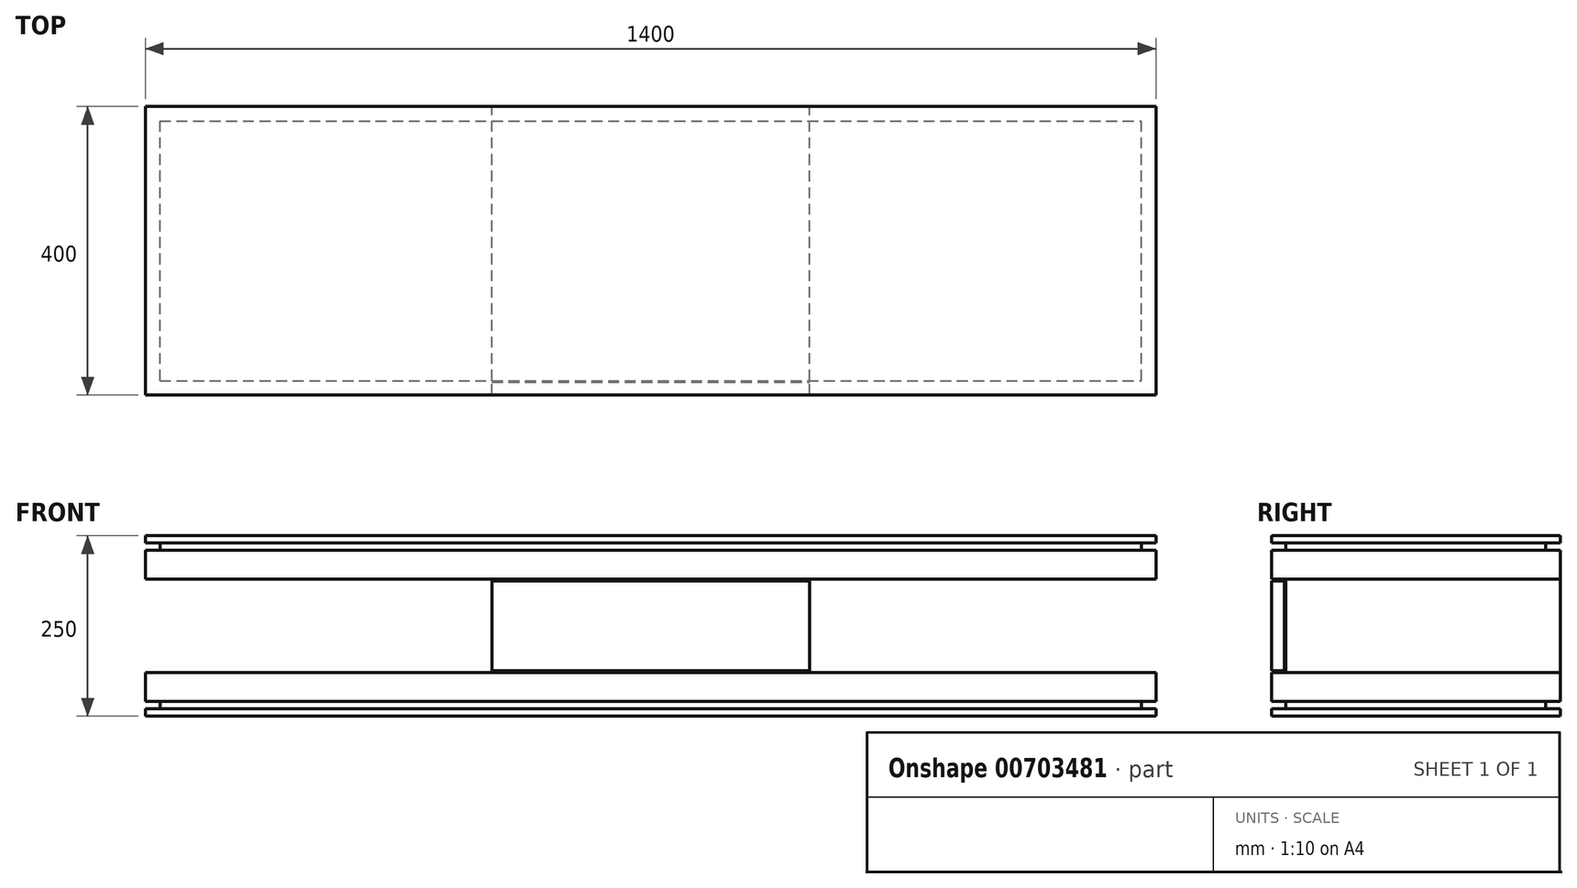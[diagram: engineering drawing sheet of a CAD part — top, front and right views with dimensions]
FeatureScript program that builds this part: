
annotation { "Feature Type Name" : "Feature", "Feature Type Description" : "" }
export const myFeature = defineFeature(function(context is Context, id is Id, definition is map)
    precondition{}
    {
        {
            var Q0;
            Q0=qCreatedBy(makeId("Front.planeOp"),FACE);
            var sketch = newSketch(context, id + "F0", { "sketchPlane" : qUnion([Q0])});
            skLineSegment(sketch, "E0.bottom", {"start": v(-700, 10) * mm, "end": v(700, 10) * mm});
            skLineSegment(sketch, "E0.top", {"start": v(-700, 0) * mm, "end": v(700, 0) * mm});
            skLineSegment(sketch, "E0.left", {"start": v(-700, 10) * mm, "end": v(-700, 0) * mm});
            skLineSegment(sketch, "E0.right", {"start": v(700, 10) * mm, "end": v(700, 0) * mm});
            skLineSegment(sketch, "E1.bottom", {"start": v(-680, 20) * mm, "end": v(680, 20) * mm});
            skLineSegment(sketch, "E1.top", {"start": v(-680, 10) * mm, "end": v(680, 10) * mm});
            skLineSegment(sketch, "E1.left", {"start": v(-680, 20) * mm, "end": v(-680, 10) * mm});
            skLineSegment(sketch, "E1.right", {"start": v(680, 20) * mm, "end": v(680, 10) * mm});
            skLineSegment(sketch, "E2", {"start": v(0, 20) * mm, "end": v(0, 10) * mm});
            skLineSegment(sketch, "E3.bottom", {"start": v(-700, 60) * mm, "end": v(700, 60) * mm});
            skLineSegment(sketch, "E3.top", {"start": v(-700, 20) * mm, "end": v(700, 20) * mm});
            skLineSegment(sketch, "E3.left", {"start": v(-700, 60) * mm, "end": v(-700, 20) * mm});
            skLineSegment(sketch, "E3.right", {"start": v(700, 60) * mm, "end": v(700, 20) * mm});
            skLineSegment(sketch, "E4", {"start": v(0, 20) * mm, "end": v(0, 60) * mm});
            skLineSegment(sketch, "E5.bottom", {"start": v(-700, 60) * mm, "end": v(-660, 60) * mm});
            skLineSegment(sketch, "E5.top", {"start": v(-700, 190) * mm, "end": v(-660, 190) * mm});
            skLineSegment(sketch, "E5.left", {"start": v(-700, 60) * mm, "end": v(-700, 190) * mm});
            skLineSegment(sketch, "E5.right", {"start": v(-660, 60) * mm, "end": v(-660, 190) * mm});
            skLineSegment(sketch, "E6.bottom", {"start": v(700, 60) * mm, "end": v(660, 60) * mm});
            skLineSegment(sketch, "E6.top", {"start": v(700, 190) * mm, "end": v(660, 190) * mm});
            skLineSegment(sketch, "E6.left", {"start": v(700, 60) * mm, "end": v(700, 190) * mm});
            skLineSegment(sketch, "E6.right", {"start": v(660, 60) * mm, "end": v(660, 190) * mm});
            skLineSegment(sketch, "E7.bottom", {"start": v(-700, 190) * mm, "end": v(700, 190) * mm});
            skLineSegment(sketch, "E7.top", {"start": v(-700, 230) * mm, "end": v(700, 230) * mm});
            skLineSegment(sketch, "E7.left", {"start": v(-700, 190) * mm, "end": v(-700, 230) * mm});
            skLineSegment(sketch, "E7.right", {"start": v(700, 190) * mm, "end": v(700, 230) * mm});
            skLineSegment(sketch, "E8.bottom", {"start": v(-680, 240) * mm, "end": v(680, 240) * mm});
            skLineSegment(sketch, "E8.top", {"start": v(-680, 230) * mm, "end": v(680, 230) * mm});
            skLineSegment(sketch, "E8.left", {"start": v(-680, 240) * mm, "end": v(-680, 230) * mm});
            skLineSegment(sketch, "E8.right", {"start": v(680, 240) * mm, "end": v(680, 230) * mm});
            skLineSegment(sketch, "E9", {"start": v(0, 240) * mm, "end": v(0, 230) * mm});
            skLineSegment(sketch, "E10.bottom", {"start": v(-700, 250) * mm, "end": v(700, 250) * mm});
            skLineSegment(sketch, "E10.top", {"start": v(-700, 240) * mm, "end": v(700, 240) * mm});
            skLineSegment(sketch, "E10.left", {"start": v(-700, 250) * mm, "end": v(-700, 240) * mm});
            skLineSegment(sketch, "E10.right", {"start": v(700, 250) * mm, "end": v(700, 240) * mm});
            skLineSegment(sketch, "E11", {"start": v(0, 250) * mm, "end": v(0, 240) * mm});
            skLineSegment(sketch, "E12", {"start": v(-660, 125) * mm, "end": v(-220, 125) * mm, "construction": true});
            skLineSegment(sketch, "E13", {"start": v(-220, 125) * mm, "end": v(220, 125) * mm, "construction": true});
            skLineSegment(sketch, "E14", {"start": v(220, 125) * mm, "end": v(660, 125) * mm, "construction": true});
            skLineSegment(sketch, "E15", {"start": v(-220, 190) * mm, "end": v(-220, 60) * mm});
            skLineSegment(sketch, "E16", {"start": v(220, 190) * mm, "end": v(220, 60) * mm});
            skLineSegment(sketch, "E17", {"start": v(-220, 187) * mm, "end": v(220, 187) * mm});
            skLineSegment(sketch, "E18", {"start": v(-220, 63) * mm, "end": v(220, 63) * mm});
            skSolve(sketch);
        }
        {
            var Q0;
            {var subQ0=sQuery(id+"F0.wireOp",EDGE,"E8.left");Q0=makeQuery(id+"F0.imprint","IMPRINT",FACE,{"disambiguationData":[TD([[makeQuery(id+"F0.imprint","IMPRINT",EDGE,{"derivedFrom":subQ0}),1.0]])]});}
            var Q1;
            {var subQ0=sQuery(id+"F0.wireOp",EDGE,"E8.right");Q1=makeQuery(id+"F0.imprint","IMPRINT",FACE,{"disambiguationData":[TD([[makeQuery(id+"F0.imprint","IMPRINT",EDGE,{"derivedFrom":subQ0}),-1.0]])]});}
            var Q2;
            {var subQ0=sQuery(id+"F0.wireOp",EDGE,"E1.left");Q2=makeQuery(id+"F0.imprint","IMPRINT",FACE,{"disambiguationData":[TD([[makeQuery(id+"F0.imprint","IMPRINT",EDGE,{"derivedFrom":subQ0}),1.0]])]});}
            var Q3;
            {var subQ0=sQuery(id+"F0.wireOp",EDGE,"E1.right");Q3=makeQuery(id+"F0.imprint","IMPRINT",FACE,{"disambiguationData":[TD([[makeQuery(id+"F0.imprint","IMPRINT",EDGE,{"derivedFrom":subQ0}),-1.0]])]});}
            extrude(context, id + "F1", {"entities" : qUnion([Q0, Q1, Q2, Q3]), "depth" : 180 * mm, "offsetDistance" : 25 * mm, "hasSecondDirection" : true, "secondDirectionOppositeDirection" : true, "secondDirectionDepth" : 180 * mm});
        }
        {
            var Q0;
            Q0=makeQuery(id+"F0.imprint","IMPRINT",FACE,{"disambiguationData":[TD([[makeQuery(id+"F0.imprint","IMPRINT",EDGE,{"derivedFrom":sQuery(id+"F0.wireOp",EDGE,"E0.top")}),1.0]])]});
            var Q1;
            Q1=makeQuery(id+"F0.imprint","IMPRINT",FACE,{"disambiguationData":[TD([[makeQuery(id+"F0.imprint","IMPRINT",EDGE,{"derivedFrom":sQuery(id+"F0.wireOp",EDGE,"E5.bottom")}),1.0]])]});
            var Q2;
            Q2=makeQuery(id+"F0.imprint","IMPRINT",FACE,{"disambiguationData":[TD([[makeQuery(id+"F0.imprint","IMPRINT",EDGE,{"derivedFrom":sQuery(id+"F0.wireOp",EDGE,"E6.bottom")}),-1.0]])]});
            var Q3;
            {var subQ0=sQuery(id+"F0.wireOp",EDGE,"E10.right");Q3=makeQuery(id+"F0.imprint","IMPRINT",FACE,{"disambiguationData":[TD([[makeQuery(id+"F0.imprint","IMPRINT",EDGE,{"derivedFrom":subQ0}),-1.0]])]});}
            var Q4;
            {var subQ0=sQuery(id+"F0.wireOp",EDGE,"E10.left");Q4=makeQuery(id+"F0.imprint","IMPRINT",FACE,{"disambiguationData":[TD([[makeQuery(id+"F0.imprint","IMPRINT",EDGE,{"derivedFrom":subQ0}),1.0]])]});}
            extrude(context, id + "F2", {"entities" : qUnion([Q0, Q1, Q2, Q3, Q4]), "depth" : 200 * mm, "offsetDistance" : 25 * mm, "hasSecondDirection" : true, "secondDirectionOppositeDirection" : true, "secondDirectionDepth" : 200 * mm});
        }
        {
            var Q0;
            {var subQ0=sQuery(id+"F0.wireOp",EDGE,"E7.left");Q0=makeQuery(id+"F0.imprint","IMPRINT",FACE,{"disambiguationData":[TD([[makeQuery(id+"F0.imprint","IMPRINT",EDGE,{"derivedFrom":subQ0}),-1.0]])]});}
            var Q1;
            {var subQ0=sQuery(id+"F0.wireOp",EDGE,"E3.left");Q1=makeQuery(id+"F0.imprint","IMPRINT",FACE,{"disambiguationData":[TD([[makeQuery(id+"F0.imprint","IMPRINT",EDGE,{"derivedFrom":subQ0}),1.0]])]});}
            var Q2;
            {var subQ0=sQuery(id+"F0.wireOp",EDGE,"E3.right");Q2=makeQuery(id+"F0.imprint","IMPRINT",FACE,{"disambiguationData":[TD([[makeQuery(id+"F0.imprint","IMPRINT",EDGE,{"derivedFrom":subQ0}),-1.0]])]});}
            extrude(context, id + "F3", {"entities" : qUnion([Q0, Q1, Q2]), "depth" : 200 * mm, "offsetDistance" : 25 * mm, "hasSecondDirection" : true, "secondDirectionOppositeDirection" : true, "secondDirectionDepth" : 200 * mm});
        }
        {
            var Q0;
            {var subQ0=sQuery(id+"F0.wireOp",EDGE,"E17");Q0=makeQuery(id+"F0.imprint","IMPRINT",FACE,{"disambiguationData":[TD([[makeQuery(id+"F0.imprint","IMPRINT",EDGE,{"derivedFrom":subQ0}),-1.0]])]});}
            extrude(context, id + "F4", {"entities" : qUnion([Q0]), "depth" : 200 * mm, "offsetDistance" : 25 * mm, "hasSecondDirection" : true, "secondDirectionOppositeDirection" : false, "secondDirectionDepth" : 182 * mm});
        }
        {
            var Q0;
            {var subQ0=sQuery(id+"F0.wireOp",EDGE,"E17");Q0=makeQuery(id+"F0.imprint","IMPRINT",FACE,{"disambiguationData":[TD([[makeQuery(id+"F0.imprint","IMPRINT",EDGE,{"derivedFrom":subQ0}),-1.0]])]});}
            var Q1;
            {var subQ3=sQuery(id+"F0.wireOp",EDGE,"E18");Q1=makeQuery(id+"F0.imprint","IMPRINT",FACE,{"disambiguationData":[TD([[makeQuery(id+"F0.imprint","IMPRINT",EDGE,{"derivedFrom":subQ3}),-1.0]])]});}
            var Q2;
            {var subQ5=sQuery(id+"F0.wireOp",EDGE,"E17");Q2=makeQuery(id+"F0.imprint","IMPRINT",FACE,{"disambiguationData":[TD([[makeQuery(id+"F0.imprint","IMPRINT",EDGE,{"derivedFrom":subQ5}),1.0]])]});}
            extrude(context, id + "F5", {"entities" : qUnion([Q0, Q1, Q2]), "depth" : 180 * mm, "offsetDistance" : 25 * mm, "hasSecondDirection" : true, "secondDirectionOppositeDirection" : true, "secondDirectionDepth" : 200 * mm});
        }
    });
